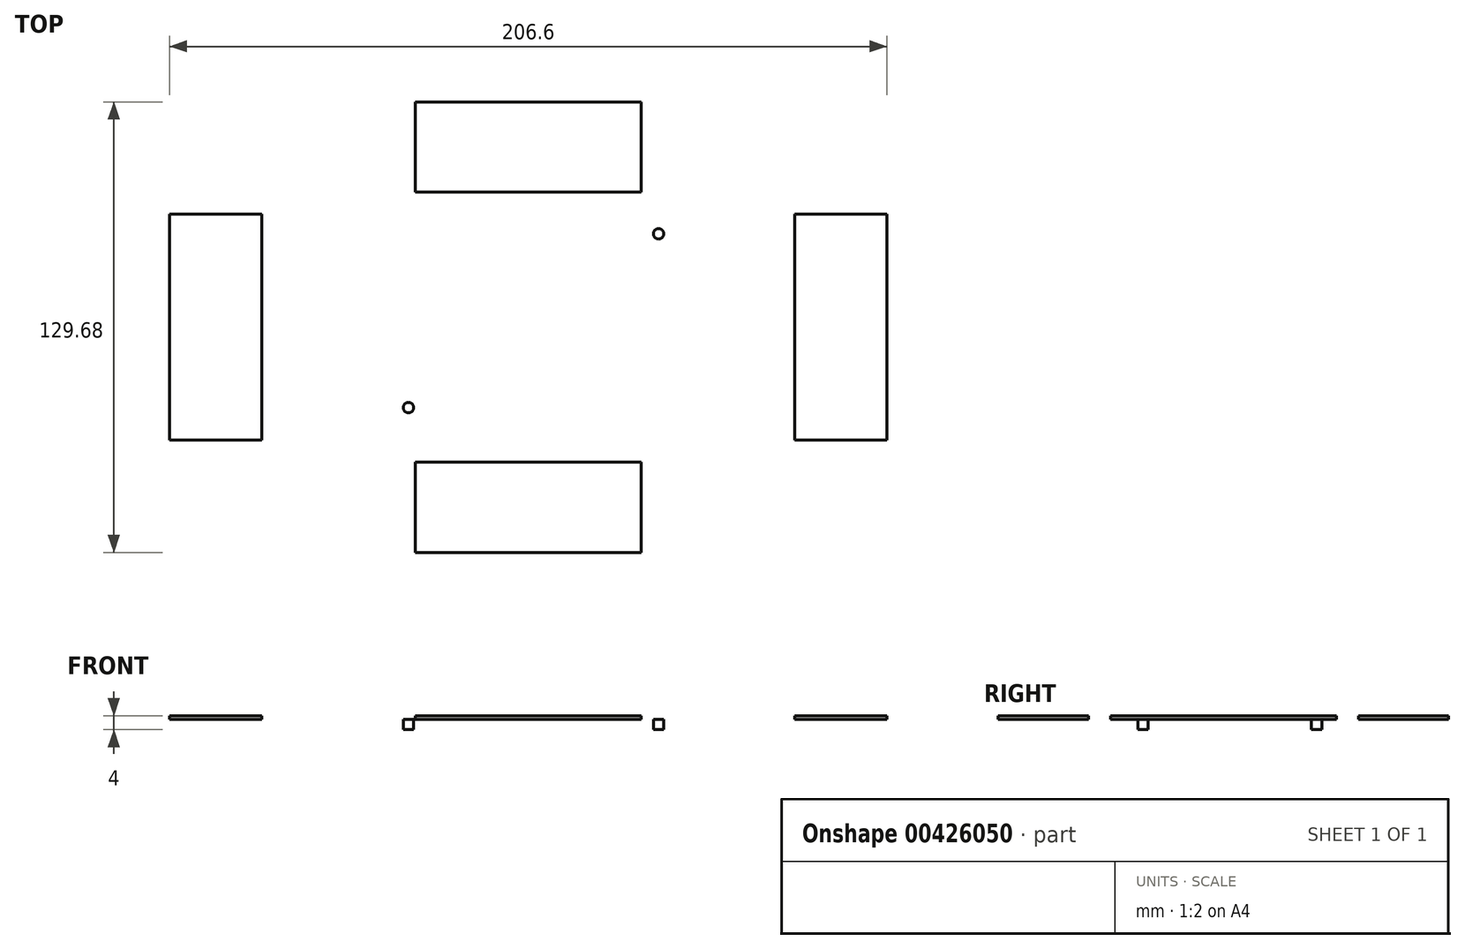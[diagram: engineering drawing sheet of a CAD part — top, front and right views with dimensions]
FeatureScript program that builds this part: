
annotation { "Feature Type Name" : "Feature", "Feature Type Description" : "" }
export const myFeature = defineFeature(function(context is Context, id is Id, definition is map)
    precondition{}
    {
        {
            var Q0;
            Q0=qCreatedBy(makeId("Top.planeOp"),FACE);
            var sketch = newSketch(context, id + "F0", { "sketchPlane" : qUnion([Q0])});
            skLineSegment(sketch, "E0.bottom", {"start": v(127, -85) * mm, "end": v(-127, -85) * mm});
            skLineSegment(sketch, "E0.top", {"start": v(127, 85) * mm, "end": v(-127, 85) * mm});
            skLineSegment(sketch, "E0.left", {"start": v(127, -85) * mm, "end": v(127, 85) * mm});
            skLineSegment(sketch, "E0.right", {"start": v(-127, -85) * mm, "end": v(-127, 85) * mm});
            skPoint(sketch, "E0.middle", {"position": v(0, 0) * mm});
            skCircle(sketch, "E1", {"center": v(-100, 50) * mm, "radius": 2.27 * mm});
            skCircle(sketch, "E2.MirrorC", {"center": v(100, 50) * mm, "radius": 2.27 * mm});
            skCircle(sketch, "E3.MirrorC", {"center": v(-100, -50) * mm, "radius": 2.27 * mm});
            skCircle(sketch, "E4.MirrorC", {"center": v(100, -50) * mm, "radius": 2.27 * mm});
            skSolve(sketch);
        }
        {
            var Q0;
            Q0=makeQuery(id+"F0.imprint","IMPRINT",FACE,{"disambiguationData":[TD([[makeQuery(id+"F0.imprint","IMPRINT",EDGE,{"derivedFrom":sQuery(id+"F0.wireOp",EDGE,"E0.bottom")}),-1.0]])]});
            extrude(context, id + "F1", {"entities" : qUnion([Q0]), "depth" : 3 * mm});
        }
        {
            var Q0;
            Q0=makeQuery(id+"F1.opExtrude","CAP_FACE",FACE,{"disambiguationData":[OSD([sQuery(id+"F0.wireOp",EDGE,"E0.bottom"),sQuery(id+"F0.wireOp",EDGE,"E0.top"),sQuery(id+"F0.wireOp",EDGE,"E0.left"),sQuery(id+"F0.wireOp",EDGE,"E0.right")])],"isStart":false});
            var sketch = newSketch(context, id + "F2", { "sketchPlane" : qUnion([Q0])});
            skLineSegment(sketch, "E5.bottom", {"start": v(119, -75) * mm, "end": v(-119, -75) * mm});
            skLineSegment(sketch, "E5.top", {"start": v(119, 75) * mm, "end": v(-119, 75) * mm});
            skLineSegment(sketch, "E5.left", {"start": v(119, -75) * mm, "end": v(119, 75) * mm});
            skLineSegment(sketch, "E5.right", {"start": v(-119, -75) * mm, "end": v(-119, 75) * mm});
            skPoint(sketch, "E5.middle", {"position": v(0, 0) * mm});
            skSolve(sketch);
        }
        {
            var Q0;
            Q0=makeQuery(id+"F2.imprint","IMPRINT",FACE,{"disambiguationData":[TD([[makeQuery(id+"F2.imprint","IMPRINT",EDGE,{"derivedFrom":sQuery(id+"F2.wireOp",EDGE,"E5.bottom")}),1.0]])]});
            extrude(context, id + "F3", {"entities" : qUnion([Q0]), "operationType" : NewBodyOperationType.ADD, "oppositeDirection" : true, "depth" : 10 * mm});
        }
        {
            var Q0;
            Q0=makeQuery(id+"F3.opExtrude","CAP_EDGE",EDGE,{"disambiguationData":[OSD([sQuery(id+"F0.wireOp",EDGE,"E0.right")])],"isStart":false});
            var Q1;
            Q1=makeQuery(id+"F3.opExtrude","CAP_EDGE",EDGE,{"disambiguationData":[OSD([sQuery(id+"F2.wireOp",EDGE,"E5.right")])],"isStart":false});
            var Q2;
            Q2=makeQuery(id+"F3.opExtrude","CAP_EDGE",EDGE,{"disambiguationData":[OSD([sQuery(id+"F2.wireOp",EDGE,"E5.top")])],"isStart":false});
            var Q3;
            Q3=makeQuery(id+"F3.opExtrude","CAP_EDGE",EDGE,{"disambiguationData":[OSD([sQuery(id+"F0.wireOp",EDGE,"E0.top")])],"isStart":false});
            var Q4;
            Q4=makeQuery(id+"F3.opExtrude","CAP_EDGE",EDGE,{"disambiguationData":[OSD([sQuery(id+"F2.wireOp",EDGE,"E5.left")])],"isStart":false});
            var Q5;
            Q5=makeQuery(id+"F3.opExtrude","CAP_EDGE",EDGE,{"disambiguationData":[OSD([sQuery(id+"F0.wireOp",EDGE,"E0.left")])],"isStart":false});
            var Q6;
            Q6=makeQuery(id+"F3.opExtrude","CAP_EDGE",EDGE,{"disambiguationData":[OSD([sQuery(id+"F2.wireOp",EDGE,"E5.bottom")])],"isStart":false});
            var Q7;
            Q7=makeQuery(id+"F1.opExtrude","CAP_EDGE",EDGE,{"disambiguationData":[OSD([sQuery(id+"F0.wireOp",EDGE,"E0.bottom")])],"isStart":true});
            var Q8;
            Q8=makeQuery(id+"F3.opExtrude","CAP_EDGE",EDGE,{"disambiguationData":[OSD([sQuery(id+"F0.wireOp",EDGE,"E0.bottom")])],"isStart":false});
            fillet(context, id + "F4", {"entities" : qUnion([Q0, Q1, Q2, Q3, Q4, Q5, Q6, Q7, Q8]), "radius" : 3 * mm, "tangentPropagation" : true, "allowEdgeOverflow" : false});
        }
        {
            var Q0;
            Q0=makeQuery(id+"F1.opExtrude","CAP_FACE",FACE,{"disambiguationData":[OSD([sQuery(id+"F0.wireOp",EDGE,"E0.bottom"),sQuery(id+"F0.wireOp",EDGE,"E0.top"),sQuery(id+"F0.wireOp",EDGE,"E0.left"),sQuery(id+"F0.wireOp",EDGE,"E0.right")])],"isStart":false});
            var sketch = newSketch(context, id + "F5", { "sketchPlane" : qUnion([Q0])});
            skCircle(sketch, "E6", {"center": v(-34.48, 26.85) * mm, "radius": 1.5 * mm});
            skCircle(sketch, "E7.MirrorC", {"center": v(37.52, 26.85) * mm, "radius": 1.5 * mm});
            skCircle(sketch, "E8.MirrorC", {"center": v(-34.48, -23.15) * mm, "radius": 1.5 * mm});
            skCircle(sketch, "E9.MirrorC", {"center": v(37.52, -23.15) * mm, "radius": 1.5 * mm});
            skSolve(sketch);
        }
        {
            var Q0;
            Q0=makeQuery(id+"F5.imprint","IMPRINT",FACE,{"disambiguationData":[TD([[makeQuery(id+"F5.imprint","IMPRINT",EDGE,{"derivedFrom":sQuery(id+"F5.wireOp",EDGE,"OjA2Dnud-UjMS-CDD4-xOqX-URSDM7NJb9P5")}),1.0]])]});
            var Q1;
            Q1=makeQuery(id+"F5.imprint","IMPRINT",FACE,{"disambiguationData":[TD([[makeQuery(id+"F5.imprint","IMPRINT",EDGE,{"derivedFrom":sQuery(id+"F5.wireOp",EDGE,"bd7eb0ad-859a-4e25-8c5d-042c519c33eb0.MirrorC")}),-1.0]])]});
            var Q2;
            Q2=makeQuery(id+"F5.imprint","IMPRINT",FACE,{"disambiguationData":[TD([[makeQuery(id+"F5.imprint","IMPRINT",EDGE,{"derivedFrom":sQuery(id+"F5.wireOp",EDGE,"E8.MirrorC")}),-1.0]])]});
            var Q3;
            Q3=makeQuery(id+"F5.imprint","IMPRINT",FACE,{"disambiguationData":[TD([[makeQuery(id+"F5.imprint","IMPRINT",EDGE,{"derivedFrom":sQuery(id+"F5.wireOp",EDGE,"E6")}),1.0]])]});
            var Q4;
            Q4=makeQuery(id+"F5.imprint","IMPRINT",FACE,{"disambiguationData":[TD([[makeQuery(id+"F5.imprint","IMPRINT",EDGE,{"derivedFrom":sQuery(id+"F5.wireOp",EDGE,"E9.MirrorC")}),1.0]])]});
            var Q5;
            Q5=makeQuery(id+"F5.imprint","IMPRINT",FACE,{"disambiguationData":[TD([[makeQuery(id+"F5.imprint","IMPRINT",EDGE,{"derivedFrom":sQuery(id+"F5.wireOp",EDGE,"E7.MirrorC")}),-1.0]])]});
            extrude(context, id + "F6", {"entities" : qUnion([Q0, Q1, Q2, Q3, Q4, Q5]), "operationType" : NewBodyOperationType.REMOVE, "oppositeDirection" : true, "depth" : 25 * mm});
        }
        {
            var Q0;
            Q0=makeQuery(id+"F1.opExtrude","CAP_FACE",FACE,{"disambiguationData":[OSD([sQuery(id+"F0.wireOp",EDGE,"E0.bottom"),sQuery(id+"F0.wireOp",EDGE,"E0.top"),sQuery(id+"F0.wireOp",EDGE,"E0.left"),sQuery(id+"F0.wireOp",EDGE,"E0.right")])],"isStart":false});
            var sketch = newSketch(context, id + "F7", { "sketchPlane" : qUnion([Q0])});
            skLineSegment(sketch, "E10.bottom", {"start": v(32.5, 38.84) * mm, "end": v(-32.5, 38.84) * mm});
            skLineSegment(sketch, "E10.top", {"start": v(32.5, 64.84) * mm, "end": v(-32.5, 64.84) * mm});
            skLineSegment(sketch, "E10.left", {"start": v(32.5, 38.84) * mm, "end": v(32.5, 64.84) * mm});
            skLineSegment(sketch, "E10.right", {"start": v(-32.5, 38.84) * mm, "end": v(-32.5, 64.84) * mm});
            skPoint(sketch, "E10.middle", {"position": v(0, 51.84) * mm});
            skLineSegment(sketch, "E11.bottom", {"start": v(103.3, -32.5) * mm, "end": v(76.7, -32.5) * mm});
            skLineSegment(sketch, "E11.top", {"start": v(103.3, 32.5) * mm, "end": v(76.7, 32.5) * mm});
            skLineSegment(sketch, "E11.left", {"start": v(103.3, -32.5) * mm, "end": v(103.3, 32.5) * mm});
            skLineSegment(sketch, "E11.right", {"start": v(76.7, -32.5) * mm, "end": v(76.7, 32.5) * mm});
            skPoint(sketch, "E11.middle", {"position": v(90, 0) * mm});
            skLineSegment(sketch, "E12.MirrorCS", {"start": v(32.5, -38.84) * mm, "end": v(-32.5, -38.84) * mm});
            skLineSegment(sketch, "E13.MirrorCS", {"start": v(-32.5, -38.84) * mm, "end": v(-32.5, -64.84) * mm});
            skLineSegment(sketch, "E14.MirrorCS", {"start": v(32.5, -64.84) * mm, "end": v(-32.5, -64.84) * mm});
            skLineSegment(sketch, "E15.MirrorCS", {"start": v(32.5, -38.84) * mm, "end": v(32.5, -64.84) * mm});
            skLineSegment(sketch, "E16.MirrorCS", {"start": v(-76.7, -32.5) * mm, "end": v(-76.7, 32.5) * mm});
            skLineSegment(sketch, "E17.MirrorCS", {"start": v(-103.3, -32.5) * mm, "end": v(-103.3, 32.5) * mm});
            skLineSegment(sketch, "E18.MirrorCS", {"start": v(-103.3, 32.5) * mm, "end": v(-76.7, 32.5) * mm});
            skLineSegment(sketch, "E19.MirrorCS", {"start": v(-103.3, -32.5) * mm, "end": v(-76.7, -32.5) * mm});
            skPoint(sketch, "E20.MirrorP", {"position": v(-90, 0) * mm});
            skPoint(sketch, "E21.MirrorP", {"position": v(0, -51.84) * mm});
            skSolve(sketch);
        }
        {
            var Q0;
            Q0=makeQuery(id+"F7.imprint","IMPRINT",FACE,{"disambiguationData":[TD([[makeQuery(id+"F7.imprint","IMPRINT",EDGE,{"derivedFrom":sQuery(id+"F7.wireOp",EDGE,"E16.MirrorCS")}),1.0]])]});
            var Q1;
            Q1=makeQuery(id+"F7.imprint","IMPRINT",FACE,{"disambiguationData":[TD([[makeQuery(id+"F7.imprint","IMPRINT",EDGE,{"derivedFrom":sQuery(id+"F7.wireOp",EDGE,"E10.bottom")}),-1.0]])]});
            var Q2;
            Q2=makeQuery(id+"F7.imprint","IMPRINT",FACE,{"disambiguationData":[TD([[makeQuery(id+"F7.imprint","IMPRINT",EDGE,{"derivedFrom":sQuery(id+"F7.wireOp",EDGE,"E12.MirrorCS")}),1.0]])]});
            var Q3;
            Q3=makeQuery(id+"F7.imprint","IMPRINT",FACE,{"disambiguationData":[TD([[makeQuery(id+"F7.imprint","IMPRINT",EDGE,{"derivedFrom":sQuery(id+"F7.wireOp",EDGE,"E11.bottom")}),-1.0]])]});
            extrude(context, id + "F8", {"entities" : qUnion([Q0, Q1, Q2, Q3]), "operationType" : NewBodyOperationType.ADD, "depth" : 1 * mm});
        }
        {
            var Q0;
            Q0=makeQuery(id+"F1.opExtrude","CAP_FACE",FACE,{"disambiguationData":[OSD([sQuery(id+"F0.wireOp",EDGE,"E0.bottom"),sQuery(id+"F0.wireOp",EDGE,"E0.top"),sQuery(id+"F0.wireOp",EDGE,"E0.left"),sQuery(id+"F0.wireOp",EDGE,"E0.right")])],"isStart":false});
            var sketch = newSketch(context, id + "F9", { "sketchPlane" : qUnion([Q0])});
            skPoint(sketch, "E22.centerSnap0", {"position": v(-103.3, 0) * mm});
            skLineSegment(sketch, "E23.bottom", {"start": v(-42.5, 46.84) * mm, "end": v(-52.5, 46.84) * mm});
            skLineSegment(sketch, "E23.top", {"start": v(-42.5, 56.84) * mm, "end": v(-52.5, 56.84) * mm});
            skLineSegment(sketch, "E23.left", {"start": v(-42.5, 46.84) * mm, "end": v(-42.5, 56.84) * mm});
            skLineSegment(sketch, "E23.right", {"start": v(-52.5, 46.84) * mm, "end": v(-52.5, 56.84) * mm});
            skPoint(sketch, "E23.middle", {"position": v(-47.5, 51.84) * mm});
            skPoint(sketch, "E23.middle.positionSnap0", {"position": v(-32.5, 51.84) * mm});
            skPoint(sketch, "E23.centerSnap0", {"position": v(-32.5, 51.84) * mm});
            skLineSegment(sketch, "E24.bottom", {"start": v(-85, -47.2) * mm, "end": v(-95, -47.2) * mm});
            skLineSegment(sketch, "E24.top", {"start": v(-85, -37.2) * mm, "end": v(-95, -37.2) * mm});
            skLineSegment(sketch, "E24.left", {"start": v(-85, -47.2) * mm, "end": v(-85, -37.2) * mm});
            skLineSegment(sketch, "E24.right", {"start": v(-95, -47.2) * mm, "end": v(-95, -37.2) * mm});
            skPoint(sketch, "E24.middle", {"position": v(-90, -42.2) * mm});
            skPoint(sketch, "E24.middle.positionSnap0", {"position": v(-90, -32.5) * mm});
            skPoint(sketch, "E24.centerSnap0", {"position": v(-90, -32.5) * mm});
            skLineSegment(sketch, "E25.bottom", {"start": v(46.37, -56.84) * mm, "end": v(36.37, -56.84) * mm});
            skLineSegment(sketch, "E25.top", {"start": v(46.37, -46.84) * mm, "end": v(36.37, -46.84) * mm});
            skLineSegment(sketch, "E25.left", {"start": v(46.37, -56.84) * mm, "end": v(46.37, -46.84) * mm});
            skLineSegment(sketch, "E25.right", {"start": v(36.37, -56.84) * mm, "end": v(36.37, -46.84) * mm});
            skPoint(sketch, "E25.middle", {"position": v(41.37, -51.84) * mm});
            skPoint(sketch, "E25.middle.positionSnap0", {"position": v(32.5, -51.84) * mm});
            skPoint(sketch, "E25.centerSnap0", {"position": v(32.5, -51.84) * mm});
            skLineSegment(sketch, "E26.bottom", {"start": v(95, 47.5) * mm, "end": v(85, 47.5) * mm});
            skLineSegment(sketch, "E26.top", {"start": v(95, 37.5) * mm, "end": v(85, 37.5) * mm});
            skLineSegment(sketch, "E26.left", {"start": v(95, 47.5) * mm, "end": v(95, 37.5) * mm});
            skLineSegment(sketch, "E26.right", {"start": v(85, 47.5) * mm, "end": v(85, 37.5) * mm});
            skPoint(sketch, "E26.middle", {"position": v(90, 42.5) * mm});
            skPoint(sketch, "E26.middle.positionSnap0", {"position": v(90, 32.5) * mm});
            skPoint(sketch, "E26.centerSnap0", {"position": v(90, 32.5) * mm});
            skSolve(sketch);
        }
        {
            var Q0;
            Q0=makeQuery(id+"F9.imprint","IMPRINT",FACE,{"disambiguationData":[TD([[makeQuery(id+"F9.imprint","IMPRINT",EDGE,{"derivedFrom":sQuery(id+"F9.wireOp",EDGE,"E23.bottom")}),-1.0]])]});
            var Q1;
            Q1=makeQuery(id+"F9.imprint","IMPRINT",FACE,{"disambiguationData":[TD([[makeQuery(id+"F9.imprint","IMPRINT",EDGE,{"derivedFrom":sQuery(id+"F9.wireOp",EDGE,"E26.bottom")}),1.0]])]});
            var Q2;
            Q2=makeQuery(id+"F9.imprint","IMPRINT",FACE,{"disambiguationData":[TD([[makeQuery(id+"F9.imprint","IMPRINT",EDGE,{"derivedFrom":sQuery(id+"F9.wireOp",EDGE,"E25.bottom")}),-1.0]])]});
            var Q3;
            Q3=makeQuery(id+"F9.imprint","IMPRINT",FACE,{"disambiguationData":[TD([[makeQuery(id+"F9.imprint","IMPRINT",EDGE,{"derivedFrom":sQuery(id+"F9.wireOp",EDGE,"E24.bottom")}),-1.0]])]});
            extrude(context, id + "F10", {"entities" : qUnion([Q0, Q1, Q2, Q3]), "operationType" : NewBodyOperationType.REMOVE, "oppositeDirection" : true, "depth" : 25 * mm});
        }
    });
